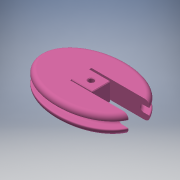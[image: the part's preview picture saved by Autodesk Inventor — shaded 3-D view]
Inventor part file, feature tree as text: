
AUTODESK INVENTOR PART (.ipt)
format: ipt  version: 2017 SP1 (Build 210196100, 196)  size: 424,960 bytes
history: native  units: in
note: dims shown in document units (in); Inventor stores cm internally (conversion verified against a paired STEP export)
features: sketch x4, extrude x2, sweep x1, chamfer x1
ambient origin geometry x8: Origin, YZ Plane, XZ Plane, XY Plane, X Axis, Y Axis, Z Axis, Center Point
bodies: Solid1 (feature_tree)
feature tree (8):
  sweep  "Sweep1"
  extrude  "Extrusion1"  Depth=0.05in
  extrude  "Extrusion2"  Depth=2.0in
  chamfer  "Chamfer1"  [1 undecoded]
  sketch  "Sketch1"  dims[d1=0.875in d5=0.25in]
  sketch  "Sketch2"  dims[d6=0.3125in d7=0.05in]
  sketch  "Sketch3"  dims[d8=0.22in d9=2.0in]
  sketch  "Sketch4"  dims[d10=1.25in d11=0.0in d12=0.0in d13=0.865in d14=0.0in d19=0.875in d20=0.0in d23=0.26in d25=0.5in d26=0.5in d27=0.865in d29=4.0in d30=0.5in d31=2.0in d32=1.02in d33=0.03in d34=0.125in d35=45.0deg]
note: 1 required parameter value undecoded (feature->parameter linkage not recoverable at this tier; creation-order binding heuristic only, values carry confidence <= 0.55)
